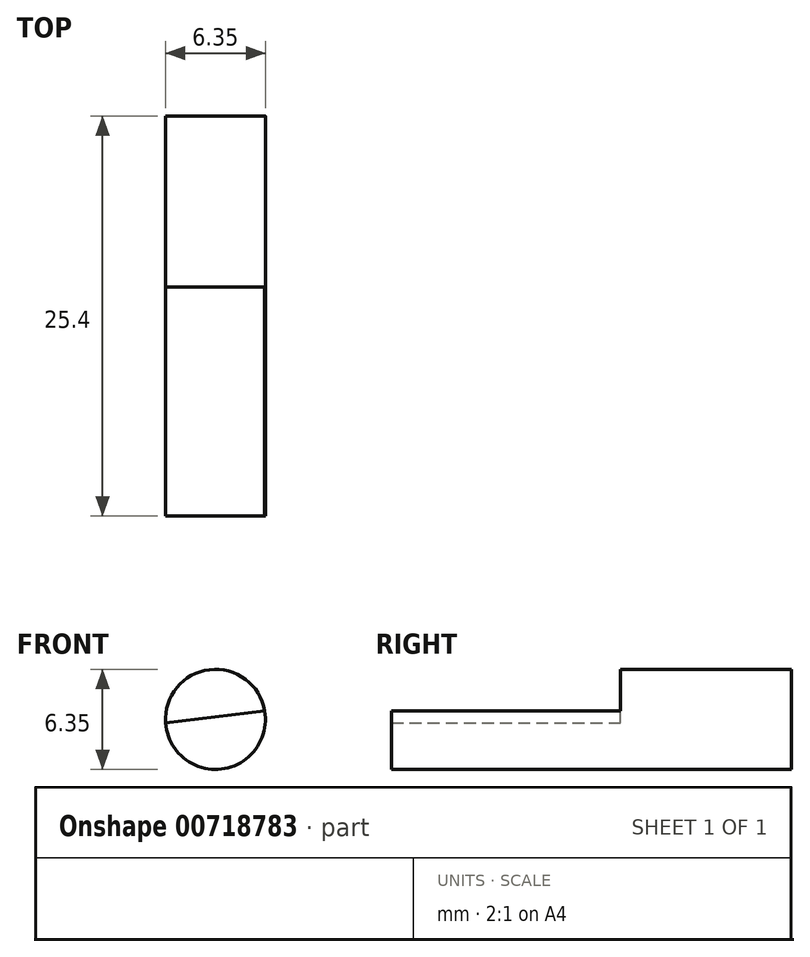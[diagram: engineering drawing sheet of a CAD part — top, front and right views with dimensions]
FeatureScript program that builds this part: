
annotation { "Feature Type Name" : "Feature", "Feature Type Description" : "" }
export const myFeature = defineFeature(function(context is Context, id is Id, definition is map)
    precondition{}
    {
        {
            var Q0;
            Q0=qCreatedBy(makeId("Front.planeOp"),FACE);
            var sketch = newSketch(context, id + "F0", { "sketchPlane" : qUnion([Q0])});
            skCircle(sketch, "E0", {"center": v(-45.57, 7.37) * mm, "radius": 3.18 * mm});
            skSolve(sketch);
        }
        {
            var Q0;
            Q0=makeQuery(id+"F0.imprint","IMPRINT",FACE,{"disambiguationData":[TD([[makeQuery(id+"F0.imprint","IMPRINT",EDGE,{"derivedFrom":sQuery(id+"F0.wireOp",EDGE,"E0")}),1.0]])]});
            extrude(context, id + "F1", {"entities" : qUnion([Q0]), "depth" : 25.4 * mm, "offsetDistance" : 25.4 * mm});
        }
        {
            var Q0;
            Q0=makeQuery(id+"F1.opExtrude","CAP_FACE",FACE,{"disambiguationData":[OSD([sQuery(id+"F0.wireOp",EDGE,"E0")])],"isStart":false});
            var sketch = newSketch(context, id + "F2", { "sketchPlane" : qUnion([Q0])});
            skLineSegment(sketch, "E1", {"start": v(-45.99, 10.83) * mm, "end": v(-45.19, 4.22) * mm});
            skSolve(sketch);
        }
        {
            var Q0;
            Q0=sQuery(id+"F2.wireOp",EDGE,"E1");
            cPlane(context, id + "F3", {"entities" : qUnion([Q0]), "cplaneType" : CPlaneType.MID_PLANE, "offset" : 25.4 * mm, "oppositeDirection" : true, "width" : 152.4 * mm, "height" : 152.4 * mm});
        }
        {
            var Q0;
            Q0=qCreatedBy(id+"F3.planeOp",FACE);
            var sketch = newSketch(context, id + "F4", { "sketchPlane" : qUnion([Q0])});
            skLineSegment(sketch, "E2.bottom", {"start": v(-49.3, 10.86) * mm, "end": v(-40.83, 10.86) * mm});
            skLineSegment(sketch, "E2.top", {"start": v(-49.3, 25.93) * mm, "end": v(-40.83, 25.93) * mm});
            skLineSegment(sketch, "E2.left", {"start": v(-49.3, 10.86) * mm, "end": v(-49.3, 25.93) * mm});
            skLineSegment(sketch, "E2.right", {"start": v(-40.83, 10.86) * mm, "end": v(-40.83, 25.93) * mm});
            skSolve(sketch);
        }
        {
            var Q0;
            Q0 = qSketchRegion(id + "F4", true);
            extrude(context, id + "F5", {"entities" : qUnion([Q0]), "operationType" : NewBodyOperationType.REMOVE, "oppositeDirection" : true, "depth" : 25.4 * mm, "offsetDistance" : 25.4 * mm});
        }
    });
